# Revit family: 3-588-xxx - Magnum Wall Sconce
name_source: partatom
category: Luminarias
units: mm (PartAtom-declared; Revit-internal decimal feet)

## family parameters
Anfitrión = Cara
Compartido = No
Corte con vacíos al cargar = No
Cota de conector redondo = Diámetro de uso
Origen de luz = Sí
Punto de cálculo de habitación = No
Tipo de pieza = Normal

## types (4) — shared parameters
Archivo de red fotométrica = 3-588-24 Magnum Vanity.ies
Cambio de temperatura de color de luz atenuada = <Ninguno>
Comentarios de vataje = 12.1 W at 120 V
Fabricante = Oxygen Lighting & Fans
Filtro de color = 16777215
Longitud de línea de emisión = 9 "
Lámpara = LED Array
Modelo = 3-588-xxx - Magnum Wall Sconce
URL = www.oxygenlighting.com
Voltage = 277 V
Ángulo de inclinación = 0.00°
zero-valued in all types: Elevación por defecto

## per-type parameters (varying)
| type | Diffuser | Metal Finish |
| 3-588-24 / Satin Nickel - Matte White Acrylic | Matte White Acrylic | 24 - Satin Nickel |
| 3-588-40 / Aged Brass - Matte White Acrylic | Matte White Acrylic | 40 - Aged Brass |
| 3-588-124 / Satin Nickel - White Opal Glass | Matte Opal Glass | 24 - Satin Nickel |
| 3-588-140 / Aged Brass - White Opal Glass | Matte Opal Glass | 40 - Aged Brass |

## geometry (parser evidence)
native form markers: Extrusion x1, Sweep x5
no freeform markers — native parametric forms only
